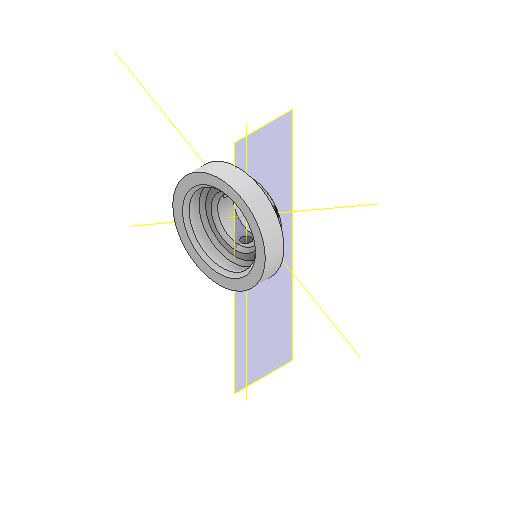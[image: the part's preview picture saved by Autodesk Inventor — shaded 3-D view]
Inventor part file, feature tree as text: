
AUTODESK INVENTOR PART (.ipt)
format: ipt  version: 2022 (Build 260153000, 153)  size: 196,608 bytes
history: native  units: mm
features: other x6, sketch x3, reference x3, extrude x2, chamfer x2, plane x1, revolve x1, pattern_circular x1, projected_geometry x1
ambient origin geometry x8: Origin, YZ Plane, XZ Plane, XY Plane, X Axis, Y Axis, Z Axis, Center Point
bodies: Volumenkörper1 (feature_tree)
feature tree (20):
  plane  "Arbeitsebene1"
  revolve  "Umdrehung1"
  extrude  "Extrusion1"  Depth=1.0mm
  pattern_circular  "Runde Anordnung1"  [2 undecoded]
  chamfer  "Fase1"  Distance=30.0mm Angle=360.0deg
  other  "Arbeitsachse1"
  other  "Arbeitsachse2"
  other  "Arbeitsachse3"
  extrude  "Extrusion4"  Depth=6.396926mm
  chamfer  "Fase3"  Distance=14.0mm
  sketch  "Skizze1"  dims[d1=6.0mm d3=1.0mm]
  reference  "Referenz4"
  sketch  "Skizze2"  dims[d4=360.0deg]
  reference  "Referenz5"
  reference  "Referenz6"
  sketch  "Skizze6"  dims[d5=2.8mm d6=10.0mm d7=0.0mm d8=30.0mm d9=360.0deg d11=0.5mm d13=14.0mm d14=8.0mm d15=10.0mm d16=1.0mm d17=2.0mm d18=45.0deg d31=20.1mm d32=5.0mm d33=0.0mm d34=1.0mm d35=2.0mm d36=45.0deg d37=0.3mm d38=6.396926mm]
  projected_geometry  "Projizierte Kontur1"
  other  "Assembly_Cube_Z-Stage_NEMA11_universal.iam"
  other  "30_Linear_Stage_NEMA11_arm_bayonetmount_v0:1"
  other  "Baugruppe2"
note: 2 required parameter values undecoded (feature->parameter linkage not recoverable at this tier; creation-order binding heuristic only, values carry confidence <= 0.55)
